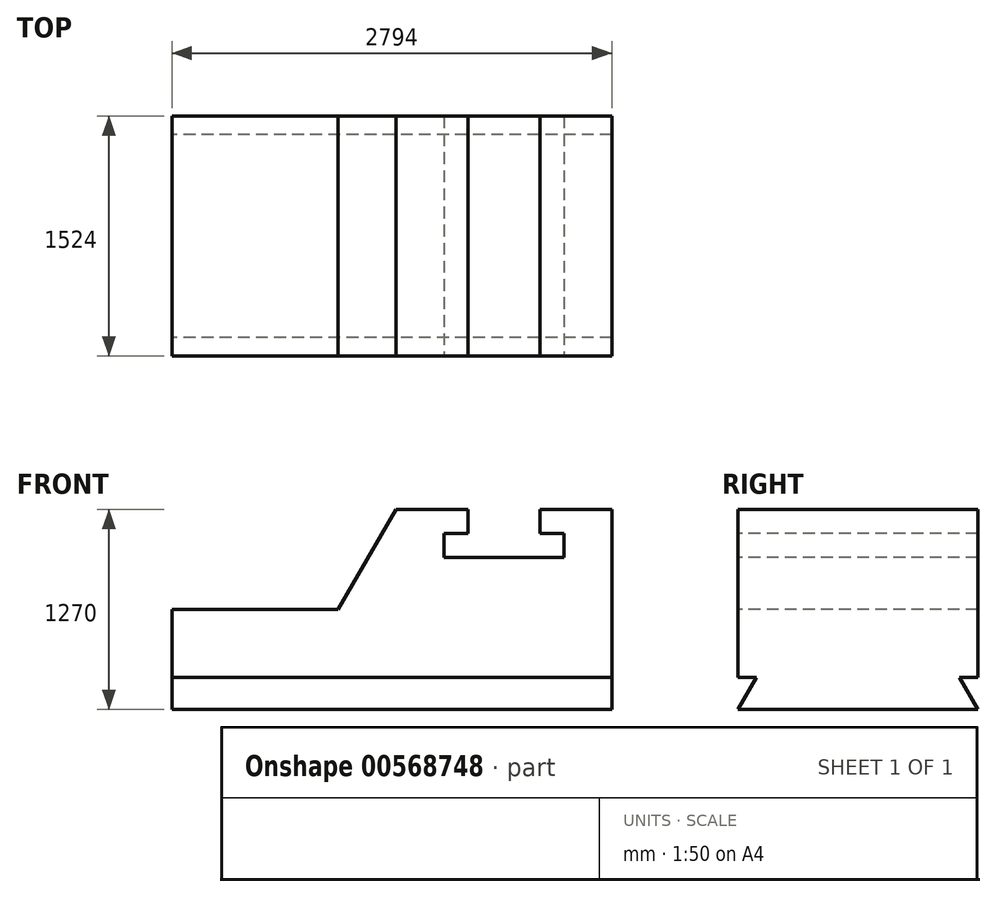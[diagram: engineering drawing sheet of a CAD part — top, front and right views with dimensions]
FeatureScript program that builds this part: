
annotation { "Feature Type Name" : "Feature", "Feature Type Description" : "" }
export const myFeature = defineFeature(function(context is Context, id is Id, definition is map)
    precondition{}
    {
        {
            var Q0;
            Q0=qCreatedBy(makeId("Front.planeOp"),FACE);
            var sketch = newSketch(context, id + "F0", { "sketchPlane" : qUnion([Q0])});
            skLineSegment(sketch, "E0", {"start": v(0, 0) * mm, "end": v(2794, 0) * mm});
            skLineSegment(sketch, "E1", {"start": v(2794, 0) * mm, "end": v(2794, 1270) * mm});
            skLineSegment(sketch, "E2", {"start": v(2794, 1270) * mm, "end": v(2336.8, 1270) * mm});
            skLineSegment(sketch, "E3", {"start": v(2336.8, 1270) * mm, "end": v(2336.8, 1117.6) * mm});
            skLineSegment(sketch, "E4", {"start": v(2336.8, 1117.6) * mm, "end": v(2489.2, 1117.6) * mm});
            skLineSegment(sketch, "E5", {"start": v(2489.2, 1117.6) * mm, "end": v(2489.2, 965.2) * mm});
            skLineSegment(sketch, "E6", {"start": v(2489.2, 965.2) * mm, "end": v(1727.2, 965.2) * mm});
            skLineSegment(sketch, "E7", {"start": v(1727.2, 965.2) * mm, "end": v(1727.2, 1117.6) * mm});
            skLineSegment(sketch, "E8", {"start": v(1727.2, 1117.6) * mm, "end": v(1879.6, 1117.6) * mm});
            skLineSegment(sketch, "E9", {"start": v(1879.6, 1117.6) * mm, "end": v(1879.6, 1270) * mm});
            skLineSegment(sketch, "E10", {"start": v(1879.6, 1270) * mm, "end": v(1422.4, 1270) * mm});
            skLineSegment(sketch, "E11", {"start": v(1422.4, 1270) * mm, "end": v(1055.78, 635) * mm});
            skLineSegment(sketch, "E12", {"start": v(0, 0) * mm, "end": v(0, 635) * mm});
            skPoint(sketch, "E13.end.orphan", {"position": v(889, 635) * mm});
            skLineSegment(sketch, "E14", {"start": v(0, 635) * mm, "end": v(1055.78, 635) * mm});
            skSolve(sketch);
        }
        {
            var Q0;
            Q0=makeQuery(id+"F0.imprint","IMPRINT",FACE,{"disambiguationData":[TD([[makeQuery(id+"F0.imprint","IMPRINT",EDGE,{"derivedFrom":sQuery(id+"F0.wireOp",EDGE,"E0")}),1.0]])]});
            extrude(context, id + "F1", {"entities" : qUnion([Q0]), "oppositeDirection" : true, "depth" : 1524 * mm, "offsetDistance" : 25.4 * mm});
        }
        {
            var Q0;
            Q0=makeQuery(id+"F1.opExtrude","SWEPT_FACE",FACE,{"disambiguationData":[OSD([sQuery(id+"F0.wireOp",EDGE,"E12")])]});
            var sketch = newSketch(context, id + "F2", { "sketchPlane" : qUnion([Q0])});
            skSolve(sketch);
        }
        {
            var Q0;
            {var subQ0=sQuery(id+"F0.wireOp",EDGE,"E12");Q0=makeQuery(id+"F2.imprint","IMPRINT",FACE,{"disambiguationData":[TD([[makeQuery(id+"F2.imprint","IMPRINT",EDGE,{"derivedFrom":makeQuery(id+"F1.opExtrude","CAP_EDGE",EDGE,{"disambiguationData":[OSD([subQ0])],"isStart":true})}),1.0]])]});}
            var sketch = newSketch(context, id + "F3", { "sketchPlane" : qUnion([Q0])});
            skLineSegment(sketch, "E15", {"start": v(-1524, 0) * mm, "end": v(-1406.68, 203.2) * mm});
            skLineSegment(sketch, "E16", {"start": v(-1406.68, 203.2) * mm, "end": v(-1524, 203.2) * mm});
            skLineSegment(sketch, "E17", {"start": v(-1524, 0) * mm, "end": v(-1524, 203.2) * mm});
            skSolve(sketch);
        }
        {
            var Q0;
            {var subQ0=sQuery(id+"F0.wireOp",EDGE,"E12");Q0=makeQuery(id+"F2.imprint","IMPRINT",FACE,{"disambiguationData":[TD([[makeQuery(id+"F2.imprint","IMPRINT",EDGE,{"derivedFrom":makeQuery(id+"F1.opExtrude","CAP_EDGE",EDGE,{"disambiguationData":[OSD([subQ0])],"isStart":true})}),1.0]])]});}
            var sketch = newSketch(context, id + "F4", { "sketchPlane" : qUnion([Q0])});
            skLineSegment(sketch, "E18", {"start": v(0, 0) * mm, "end": v(-117.32, 203.2) * mm});
            skLineSegment(sketch, "E19", {"start": v(-117.32, 203.2) * mm, "end": v(0, 203.2) * mm});
            skLineSegment(sketch, "E20", {"start": v(0, 203.2) * mm, "end": v(0, 0) * mm});
            skSolve(sketch);
        }
        {
            var Q0;
            Q0 = qSketchRegion(id + "F4", true);
            extrude(context, id + "F5", {"entities" : qUnion([Q0]), "operationType" : NewBodyOperationType.REMOVE, "endBound" : BoundingType.THROUGH_ALL, "oppositeDirection" : true, "depth" : 25.4 * mm, "offsetDistance" : 25.4 * mm});
        }
        {
            var Q0;
            {var subQ0=sQuery(id+"F0.wireOp",EDGE,"E12");Q0=makeQuery(id+"F2.imprint","IMPRINT",FACE,{"disambiguationData":[TD([[makeQuery(id+"F2.imprint","IMPRINT",EDGE,{"derivedFrom":makeQuery(id+"F1.opExtrude","CAP_EDGE",EDGE,{"disambiguationData":[OSD([subQ0])],"isStart":true})}),1.0]])]});}
            var sketch = newSketch(context, id + "F6", { "sketchPlane" : qUnion([Q0])});
            skLineSegment(sketch, "E21", {"start": v(-1524, 0) * mm, "end": v(-1406.68, 203.2) * mm});
            skLineSegment(sketch, "E22", {"start": v(-1406.68, 203.2) * mm, "end": v(-1524, 203.2) * mm});
            skLineSegment(sketch, "E23", {"start": v(-1524, 203.2) * mm, "end": v(-1524, 0) * mm});
            skSolve(sketch);
        }
        {
            var Q0;
            Q0 = qSketchRegion(id + "F6", true);
            extrude(context, id + "F7", {"entities" : qUnion([Q0]), "operationType" : NewBodyOperationType.REMOVE, "endBound" : BoundingType.THROUGH_ALL, "oppositeDirection" : true, "depth" : 25.4 * mm, "offsetDistance" : 25.4 * mm});
        }
    });
